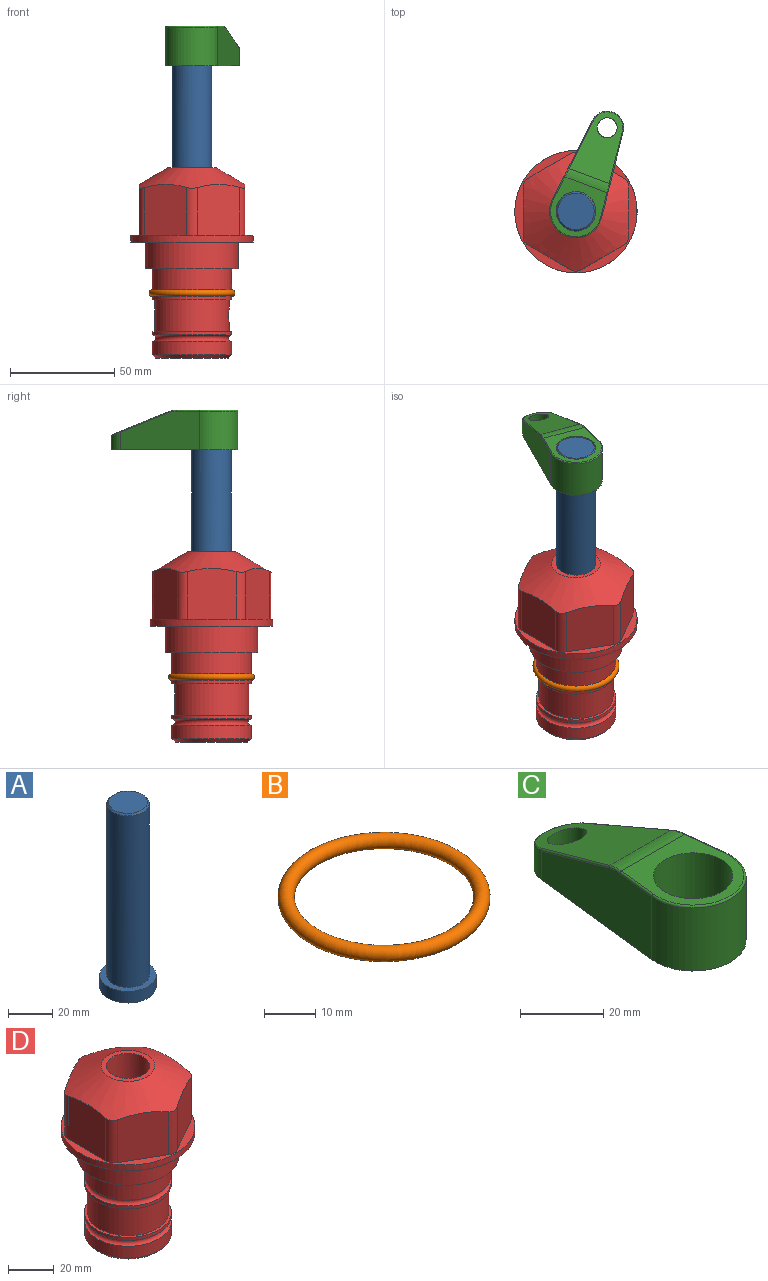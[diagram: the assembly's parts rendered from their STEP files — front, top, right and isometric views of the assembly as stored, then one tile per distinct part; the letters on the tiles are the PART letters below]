
ASSEMBLY  parts=4 mates=3
PART A: 6 faces, bbox 25.4x25.4x101.6 mm
  f0: plane 17.46x17.46mm, normal (0,0,1), area 239.5mm2, adj f5
  f1: plane 25.4x25.4mm, normal (0,0,-1), area 506.7mm2, adj f2
  f2: cylinder r=12.7mm len=25.4mm, axis (0,0,1), area 506.7mm2, adj f1,f3
  f3: plane 25.4x25.4mm, normal (0,0,1), area 221.7mm2, adj f2,f4
  f4: cylinder r=9.53mm len=94.46mm, axis (0,0,1), area 5653mm2, adj f3,f5
  f5: cone r=8.73mm half-angle=45deg, axis (0,0,-1), area 64.4mm2, adj f0,f4
PART B: 1 faces, bbox 44.7x44.7x3.2 mm
  f0: torus R=19.05mm, axis (0,0,1), area 1193.9mm2
PART C: 44 faces, bbox 27.5x64.5x19.1 mm
  f0: plane 2.3x0.95mm, normal (0,0,-1), area 1mm2, adj f25,f30,f34
  f1: plane 63.5x25.4mm, normal (0,0,-1), area 561.7mm2, adj f2,f3,f4,f5,f6,f7,f19,f20
  f2: cylinder r=12.7mm len=25.4mm, axis (0,0,-1), area 792.2mm2, adj f1,f3,f5,f13
  f3: plane 42.33x18.54mm, normal (0.99,0.11,0), area 647mm2, adj f1,f2,f4,f11,f12,f14
  f4: cylinder r=7.94mm len=15.78mm, axis (0,0,-1), area 158.6mm2, adj f1,f3,f5,f16
  f5: plane 42.33x18.54mm, normal (-0.99,0.11,0), area 647mm2, adj f1,f2,f4,f15,f17,f18
  f6: cylinder r=9.53mm len=19.05mm, axis (0,0,-1), area 1140.1mm2, adj f1,f8
  f7: cylinder r=4.76mm len=10.98mm, axis (0,0,-1), area 276.1mm2, adj f1,f9
  f8: plane 25.83x24.38mm, normal (0,0,1), area 262.2mm2, adj f6,f10,f11,f13,f15
  f9: plane 32.49x20.55mm, normal (0,0.34,0.94), area 489.9mm2, adj f7,f10,f14,f16,f18
  f10: cylinder r=12.7mm len=21.49mm, axis (-1,0,0), area 93.2mm2, adj f8,f9,f12,f17
  f11: cylinder r=0.51mm len=12.34mm, axis (0.11,-0.99,0), area 9.9mm2, adj f3,f8,f12,f13
  f12: bspline ~7.62x1.64mm, area 3.5mm2, adj f3,f10,f11,f14
  f13: torus R=12.19mm, axis (0,0,1), area 33.6mm2, adj f2,f8,f11,f15
  f14: cylinder r=0.51mm len=26.01mm, axis (0.1,-0.93,0.34), area 21.6mm2, adj f3,f9,f12,f16
  f15: cylinder r=0.51mm len=12.34mm, axis (0.11,0.99,0), area 9.9mm2, adj f5,f8,f13,f17
  f16: bspline ~15.78x7.05mm, area 15.7mm2, adj f4,f9,f14,f18
  f17: bspline ~7.62x1.64mm, area 3.5mm2, adj f5,f10,f15,f18
  f18: cylinder r=0.51mm len=26.01mm, axis (0.1,0.93,-0.34), area 21.6mm2, adj f5,f9,f16,f17
  f19: plane 21.6x14.29mm, normal (-0.99,-0.11,0), area 242.6mm2, adj f1,f26,f28,f34,f36,f38
  f20: plane 21.6x14.29mm, normal (0.99,-0.11,0), area 242.6mm2, adj f1,f27,f29,f37,f39,f41
  f21: cylinder r=12.7mm len=14.29mm, axis (0,0,-1), area 173.2mm2, adj f1,f26,f27,f30,f31,f33
  f22: cylinder r=7.94mm len=7.63mm, axis (0,0,-1), area 53.8mm2, adj f1,f28,f29,f42
  f23: plane 2.3x0.95mm, normal (0,0,-1), area 1mm2, adj f25,f33,f37
  f24: plane 17.94x12.32mm, normal (0,-0.34,-0.94), area 191.2mm2, adj f25,f38,f41,f42
  f25: cylinder r=9.53mm len=12.93mm, axis (-1,0,0), area 37.5mm2, adj f0,f23,f24,f31,f36,f39
  f26: cylinder r=1.59mm len=14.29mm, axis (0,0,-1), area 49mm2, adj f1,f19,f21,f32
  f27: cylinder r=1.59mm len=14.29mm, axis (0,0,-1), area 49mm2, adj f1,f20,f21,f35
  f28: cylinder r=1.59mm len=7.28mm, axis (0,0,-1), area 22.1mm2, adj f1,f19,f22,f40
  f29: cylinder r=1.59mm len=7.28mm, axis (0,0,-1), area 22.1mm2, adj f1,f20,f22,f43
  f30: torus R=14.29mm, axis (0,0,1), area 5.8mm2, adj f0,f21,f31,f32
  f31: bspline ~11.06x2.73mm, area 20.8mm2, adj f21,f25,f30,f33
  f32: sphere r=1.59mm, area 5.4mm2, adj f26,f30,f34
  f33: torus R=14.29mm, axis (0,0,1), area 5.8mm2, adj f21,f23,f31,f35
  f34: cylinder r=1.59mm len=1.68mm, axis (-0.11,0.99,0), area 2.4mm2, adj f0,f19,f32,f36
  f35: sphere r=1.59mm, area 5.4mm2, adj f27,f33,f37
  f36: bspline ~5.82x2.33mm, area 7.7mm2, adj f19,f25,f34,f38
  f37: cylinder r=1.59mm len=1.68mm, axis (0.11,0.99,0), area 2.4mm2, adj f20,f23,f35,f39
  f38: cylinder r=1.59mm len=18.33mm, axis (0.1,-0.93,0.34), area 46.7mm2, adj f19,f24,f36,f40
  f39: bspline ~5.82x2.33mm, area 7.7mm2, adj f20,f25,f37,f41
  f40: sphere r=1.59mm, area 3.6mm2, adj f28,f38,f42
  f41: cylinder r=1.59mm len=18.33mm, axis (0.1,0.93,-0.34), area 46.7mm2, adj f20,f24,f39,f43
  f42: bspline ~8.31x1.84mm, area 15.3mm2, adj f22,f24,f40,f43
  f43: sphere r=1.59mm, area 3.6mm2, adj f29,f41,f42
PART D: 36 faces, bbox 58.7x58.7x91.2 mm
  f0: cylinder r=17.78mm len=35.56mm, axis (0,0,1), area 1670.8mm2, adj f23,f24,f31
  f1: cylinder r=19.05mm len=38.1mm, axis (0,0,1), area 1191.9mm2, adj f26,f27,f30
  f2: plane 58.66x58.66mm, normal (0,0,-1), area 1150.6mm2, adj f3,f28
  f3: cylinder r=29.33mm len=58.66mm, axis (0,0,-1), area 585.1mm2, adj f2,f4
  f4: plane 58.66x58.66mm, normal (0,0,1), area 475.9mm2, adj f3,f5,f6,f7,f8,f9,f10,f11
  f5: plane 24.5x20.32mm, normal (-0.5,0.87,0), area 562.8mm2, adj f4,f15,f16,f17
  f6: plane 24.5x20.32mm, normal (0.5,0.87,0), area 562.8mm2, adj f4,f14,f15,f17
  f7: plane 24.5x23.48mm, normal (1,0,0), area 562.8mm2, adj f4,f13,f14,f17
  f8: plane 24.5x20.32mm, normal (0.5,-0.87,0), area 562.8mm2, adj f4,f12,f13,f17
  f9: plane 24.5x20.32mm, normal (-0.5,-0.87,0), area 562.8mm2, adj f4,f11,f12,f17
  f10: plane 24.5x23.48mm, normal (-1,0,0), area 562.8mm2, adj f4,f11,f16,f17
  f11: cylinder r=5.08mm len=23.01mm, axis (0,0,-1), area 121.2mm2, adj f4,f9,f10,f17
  f12: cylinder r=5.08mm len=23.01mm, axis (0,0,-1), area 121.2mm2, adj f4,f8,f9,f17
  f13: cylinder r=5.08mm len=23.01mm, axis (0,0,-1), area 121.2mm2, adj f4,f7,f8,f17
  f14: cylinder r=5.08mm len=23.01mm, axis (0,0,-1), area 121.2mm2, adj f4,f6,f7,f17
  f15: cylinder r=5.08mm len=23.01mm, axis (0,0,-1), area 121.2mm2, adj f4,f5,f6,f17
  f16: cylinder r=5.08mm len=23.01mm, axis (0,0,-1), area 121.2mm2, adj f4,f5,f10,f17
  f17: cone r=11.73mm half-angle=60deg, axis (0,0,-1), area 2071.8mm2, adj f5,f6,f7,f8,f9,f10,f11,f12
  f18: plane 23.46x23.46mm, normal (0,0,1), area 147.4mm2, adj f17,f35
  f19: plane 34.93x34.93mm, normal (0,0,-1), area 958mm2, adj f29
  f20: cylinder r=19.05mm len=38.1mm, axis (0,0,1), area 760.1mm2, adj f21,f29
  f21: torus R=19.05mm, axis (0,0,1), area 565.3mm2, adj f20,f22
  f22: cylinder r=19.05mm len=38.1mm, axis (0,0,1), area 190mm2, adj f21,f23
  f23: plane 38.1x38.1mm, normal (0,0,1), area 146.9mm2, adj f0,f22
  f24: plane 38.1x38.1mm, normal (0,0,-1), area 146.9mm2, adj f0,f25
  f25: cylinder r=19.05mm len=38.1mm, axis (0,0,1), area 190mm2, adj f24,f26
  f26: torus R=19.05mm, axis (0,0,1), area 565.3mm2, adj f1,f25
  f27: plane 44.45x44.45mm, normal (0,0,-1), area 411.7mm2, adj f1,f28
  f28: cylinder r=22.23mm len=44.45mm, axis (0,0,1), area 1773.5mm2, adj f2,f27
  f29: cone r=19.05mm half-angle=45deg, axis (0,0,1), area 257.5mm2, adj f19,f20
  f30: cylinder r=3.17mm len=6.75mm, axis (-1,0,0), area 128mm2, adj f1,f33
  f31: cylinder r=3.17mm len=6.35mm, axis (-1,0,0), area 102.5mm2, adj f0,f33
  f32: plane 25.4x25.4mm, normal (0,0,1), area 506.7mm2, adj f33
  f33: cylinder r=12.7mm len=66.42mm, axis (0,0,-1), area 5236.2mm2, adj f30,f31,f32,f34
  f34: cone r=9.53mm half-angle=30deg, axis (0,0,-1), area 443.4mm2, adj f33,f35
  f35: cylinder r=9.53mm len=19.05mm, axis (0,0,-1), area 849mm2, adj f18,f34
PLACE A rot(axis=(0,0,1),69.5deg) t=(0,0,30.03)mm
PLACE B at identity
PLACE C rot(axis=(0,0,-1),20.5deg) t=(0,0,84.64)mm
PLACE D at identity fixed
MATE cylindrical C.f2 <-> A.f2  axis (0,0,-1) through (0,0,103.69)mm
MATE slider C.f2 <-> A.f2  axis (0,0,-1) through (0,0,103.69)mm
MATE cylindrical A.f2 <-> D.f0  axis (0,0,1) through (0,0,55.67)mm
